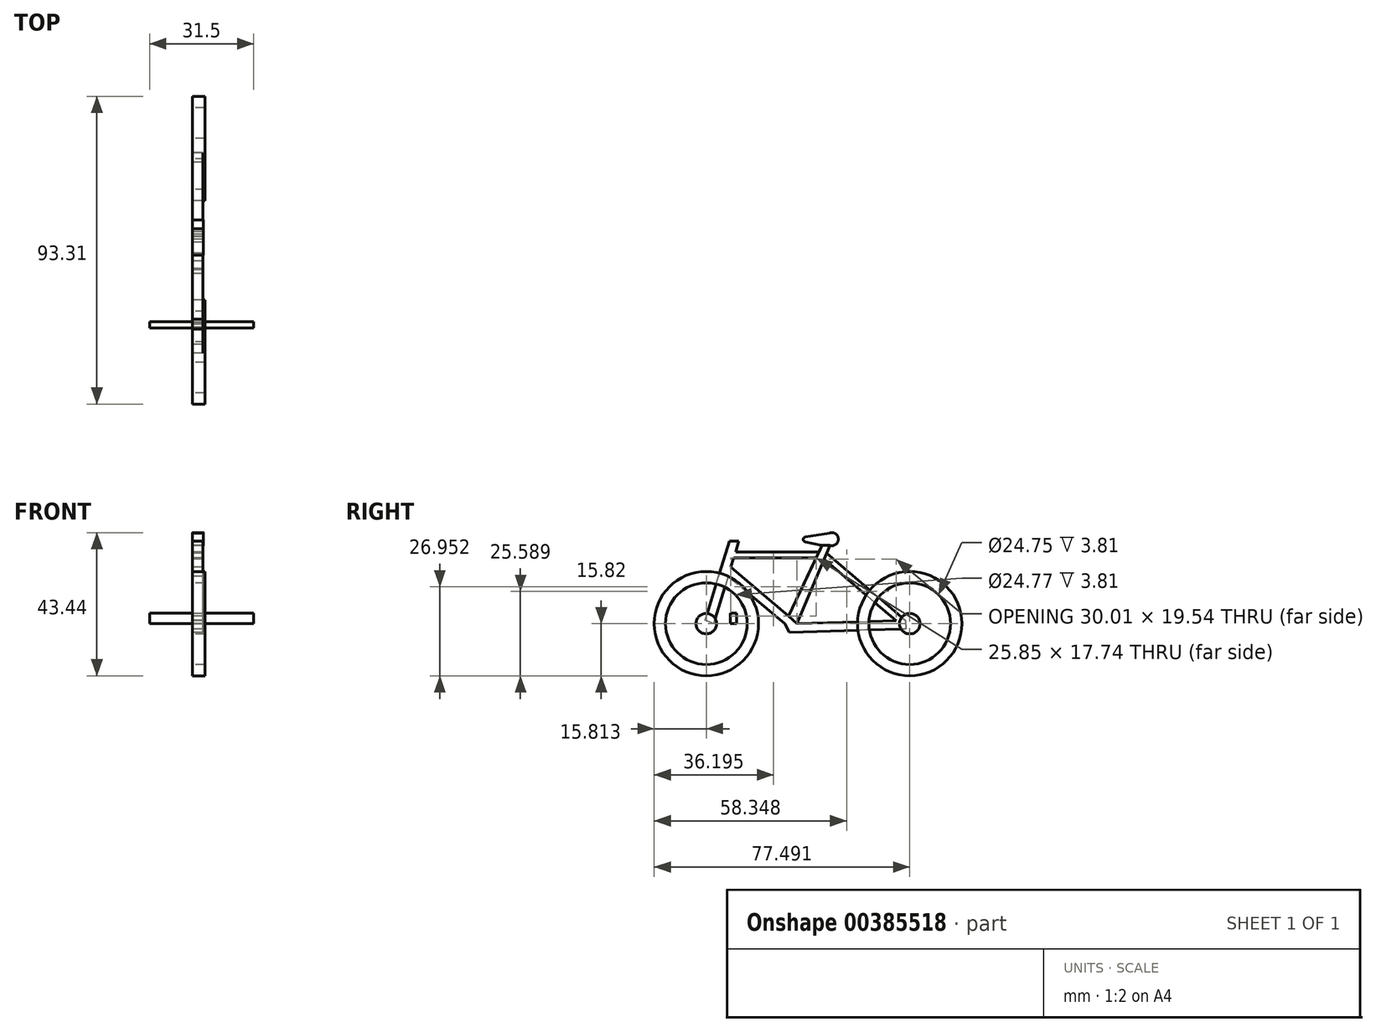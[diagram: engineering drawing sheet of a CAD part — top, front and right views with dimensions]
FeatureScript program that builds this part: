
annotation { "Feature Type Name" : "Feature", "Feature Type Description" : "" }
export const myFeature = defineFeature(function(context is Context, id is Id, definition is map)
    precondition{}
    {
        {
            var Q0;
            Q0=qCreatedBy(makeId("Right.planeOp"),FACE);
            var sketch = newSketch(context, id + "F0", { "sketchPlane" : qUnion([Q0])});
            skCircle(sketch, "E0", {"center": v(-41.44, 0) * mm, "radius": 15.81 * mm});
            skCircle(sketch, "E1", {"center": v(-41.44, 0) * mm, "radius": 12.38 * mm});
            skCircle(sketch, "E2", {"center": v(-41.44, 0) * mm, "radius": 3.1 * mm});
            skSolve(sketch);
        }
        {
            var Q0;
            Q0=qCreatedBy(makeId("Right.planeOp"),FACE);
            var sketch = newSketch(context, id + "F1", { "sketchPlane" : qUnion([Q0])});
            skCircle(sketch, "E3", {"center": v(20.24, 0) * mm, "radius": 15.82 * mm});
            skCircle(sketch, "E4", {"center": v(20.24, 0) * mm, "radius": 12.38 * mm});
            skCircle(sketch, "E5", {"center": v(20.24, 0) * mm, "radius": 3.11 * mm});
            skSolve(sketch);
        }
        {
            var Q0;
            Q0=makeQuery(id+"F0.imprint","IMPRINT",FACE,{"disambiguationData":[TD([[makeQuery(id+"F0.imprint","IMPRINT",EDGE,{"derivedFrom":sQuery(id+"F0.wireOp",EDGE,"E0")}),1.0]])]});
            var Q1;
            Q1=makeQuery(id+"F0.imprint","IMPRINT",FACE,{"disambiguationData":[TD([[makeQuery(id+"F0.imprint","IMPRINT",EDGE,{"derivedFrom":sQuery(id+"F0.wireOp",EDGE,"E2")}),1.0]])]});
            extrude(context, id + "F2", {"entities" : qUnion([Q0, Q1]), "depth" : 3.8 * mm});
        }
        {
            var Q0;
            Q0=makeQuery(id+"F1.imprint","IMPRINT",FACE,{"disambiguationData":[TD([[makeQuery(id+"F1.imprint","IMPRINT",EDGE,{"derivedFrom":sQuery(id+"F1.wireOp",EDGE,"E3")}),1.0]])]});
            var Q1;
            Q1=makeQuery(id+"F1.imprint","IMPRINT",FACE,{"disambiguationData":[TD([[makeQuery(id+"F1.imprint","IMPRINT",EDGE,{"derivedFrom":sQuery(id+"F1.wireOp",EDGE,"E5")}),1.0]])]});
            extrude(context, id + "F3", {"entities" : qUnion([Q0, Q1]), "depth" : 3.8 * mm});
        }
        {
            var Q0;
            Q0=qCreatedBy(makeId("Right.planeOp"),FACE);
            var sketch = newSketch(context, id + "F4", { "sketchPlane" : qUnion([Q0])});
            skLineSegment(sketch, "E6", {"start": v(-41.78, 1) * mm, "end": v(-34.43, 25.06) * mm});
            skLineSegment(sketch, "E7", {"start": v(-34.43, 25.06) * mm, "end": v(-31.57, 25.06) * mm});
            skLineSegment(sketch, "E8", {"start": v(-31.57, 25.06) * mm, "end": v(-39.2, 0) * mm});
            skLineSegment(sketch, "E9", {"start": v(-39.2, 0) * mm, "end": v(-41.78, 1) * mm});
            skLineSegment(sketch, "E10", {"start": v(-33.98, 17.13) * mm, "end": v(-13.9, 0) * mm});
            skLineSegment(sketch, "E11", {"start": v(-13.9, 0) * mm, "end": v(-17.63, 0) * mm});
            skLineSegment(sketch, "E12", {"start": v(-17.63, 0) * mm, "end": v(-34.84, 14.33) * mm});
            skLineSegment(sketch, "E13", {"start": v(-34.84, 14.33) * mm, "end": v(-33.98, 17.13) * mm});
            skLineSegment(sketch, "E14", {"start": v(-13.9, 0) * mm, "end": v(18.94, 1) * mm});
            skLineSegment(sketch, "E15", {"start": v(18.94, 1) * mm, "end": v(19.02, -1.58) * mm});
            skLineSegment(sketch, "E16", {"start": v(19.02, -1.58) * mm, "end": v(-16.18, -2.65) * mm});
            skLineSegment(sketch, "E17", {"start": v(-16.18, -2.65) * mm, "end": v(-17.63, 0) * mm});
            skLineSegment(sketch, "E18", {"start": v(-17.63, 0) * mm, "end": v(-6.36, 23.72) * mm});
            skLineSegment(sketch, "E19", {"start": v(-6.36, 23.72) * mm, "end": v(-3.97, 23.72) * mm});
            skLineSegment(sketch, "E20", {"start": v(-3.97, 23.72) * mm, "end": v(-13.9, 0) * mm});
            skLineSegment(sketch, "E21", {"start": v(19.02, -1.58) * mm, "end": v(-5.73, 19.54) * mm});
            skLineSegment(sketch, "E22", {"start": v(-5.73, 19.54) * mm, "end": v(-4.97, 21.35) * mm});
            skLineSegment(sketch, "E23", {"start": v(-4.97, 21.35) * mm, "end": v(18.94, 1) * mm});
            skLineSegment(sketch, "E24", {"start": v(-7.28, 21.8) * mm, "end": v(-32.56, 21.8) * mm});
            skLineSegment(sketch, "E25", {"start": v(-32.56, 21.8) * mm, "end": v(-33.1, 20) * mm});
            skLineSegment(sketch, "E26", {"start": v(-33.1, 20) * mm, "end": v(-8.13, 20) * mm});
            skLineSegment(sketch, "E27", {"start": v(-8.13, 20) * mm, "end": v(-7.28, 21.8) * mm});
            skSolve(sketch);
        }
        {
            var Q0;
            {var subQ0=sQuery(id+"F4.wireOp",EDGE,"E19");Q0=makeQuery(id+"F4.imprint","IMPRINT",FACE,{"disambiguationData":[TD([[makeQuery(id+"F4.imprint","IMPRINT",EDGE,{"derivedFrom":subQ0}),-1.0]])]});}
            extrude(context, id + "F5", {"entities" : qUnion([Q0]), "depth" : 3.17 * mm});
        }
        {
            var Q0;
            Q0 = qSketchRegion(id + "F4", true);
            extrude(context, id + "F6", {"entities" : qUnion([Q0]), "depth" : 3.17 * mm});
        }
        {
            var Q0;
            Q0=qCreatedBy(makeId("Top.planeOp"),FACE);
            var sketch = newSketch(context, id + "F7", { "sketchPlane" : qUnion([Q0])});
            skLineSegment(sketch, "E28.bottom", {"start": v(-12.98, -32.27) * mm, "end": v(18.52, -32.27) * mm});
            skLineSegment(sketch, "E28.top", {"start": v(-12.98, -34.18) * mm, "end": v(18.52, -34.18) * mm});
            skLineSegment(sketch, "E28.left", {"start": v(-12.98, -32.27) * mm, "end": v(-12.98, -34.18) * mm});
            skLineSegment(sketch, "E28.right", {"start": v(18.52, -32.27) * mm, "end": v(18.52, -34.18) * mm});
            skSolve(sketch);
        }
        {
            var Q0;
            Q0=makeQuery(id+"F7.imprint","IMPRINT",FACE,{"disambiguationData":[TD([[makeQuery(id+"F7.imprint","IMPRINT",EDGE,{"derivedFrom":sQuery(id+"F7.wireOp",EDGE,"E28.bottom")}),-1.0]])]});
            extrude(context, id + "F8", {"entities" : qUnion([Q0]), "depth" : 3.17 * mm});
        }
        {
            var Q0;
            Q0=qCreatedBy(makeId("Right.planeOp"),FACE);
            var sketch = newSketch(context, id + "F9", { "sketchPlane" : qUnion([Q0])});
            skArc(sketch, "E29", {"start": v(-4.08, 23.77) * mm, "mid": v(-1.4, 25.64) * mm, "end": v(-4.08, 27.5) * mm});
            skLineSegment(sketch, "E30", {"start": v(-4.08, 27.5) * mm, "end": v(-11.44, 26.26) * mm});
            skArc(sketch, "E31", {"start": v(-11.44, 26.26) * mm, "mid": v(-12.04, 25.54) * mm, "end": v(-11.44, 24.82) * mm});
            skLineSegment(sketch, "E32", {"start": v(-11.44, 24.82) * mm, "end": v(-6.57, 23.77) * mm});
            skLineSegment(sketch, "E33", {"start": v(-6.57, 23.77) * mm, "end": v(-4.08, 23.77) * mm});
            skSolve(sketch);
        }
        {
            var Q0;
            Q0=makeQuery(id+"F9.imprint","IMPRINT",FACE,{"disambiguationData":[TD([[makeQuery(id+"F9.imprint","IMPRINT",EDGE,{"derivedFrom":sQuery(id+"F9.wireOp",EDGE,"E29")}),1.0]])]});
            extrude(context, id + "F10", {"entities" : qUnion([Q0]), "depth" : 3.3 * mm});
        }
    });
